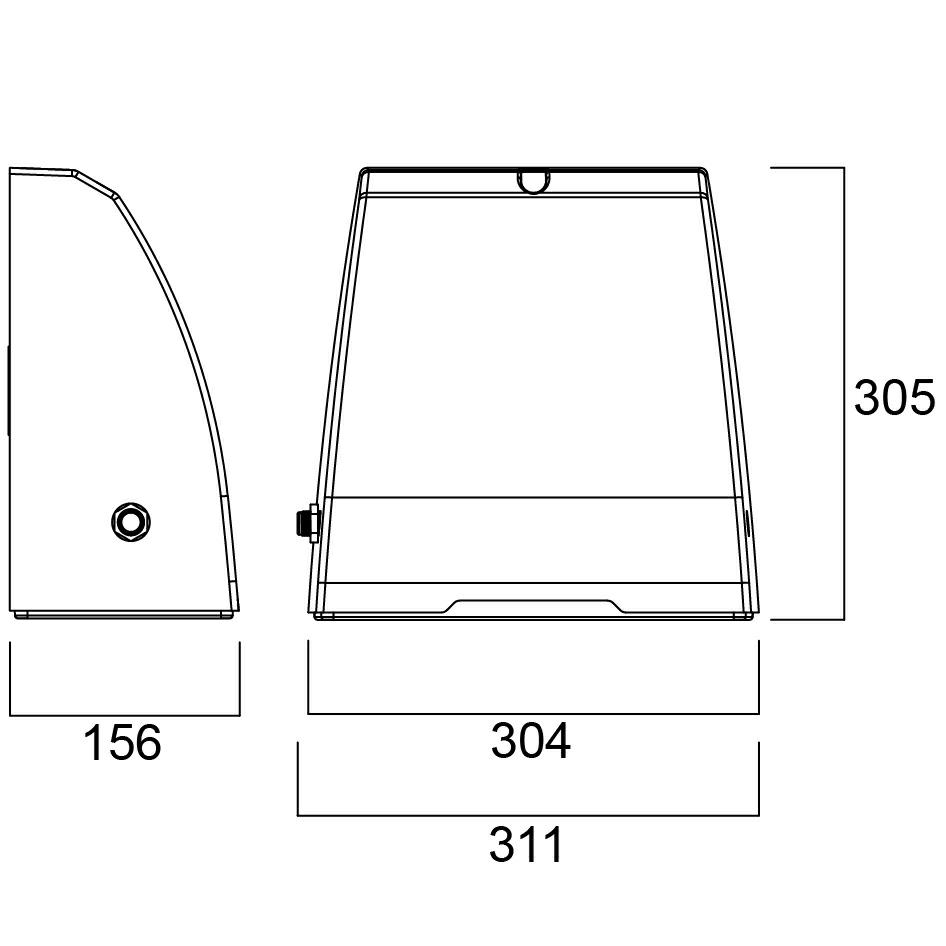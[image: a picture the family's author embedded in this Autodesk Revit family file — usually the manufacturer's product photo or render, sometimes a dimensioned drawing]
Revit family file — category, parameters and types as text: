
# Revit family: 0049945_EM mode
name_source: partatom
category: Lighting Fixtures
revit_build: Autodesk Revit 2018 (Build: 20170223_1515(x64)
units: mm (PartAtom-declared; Revit-internal decimal feet)

## family parameters
Cut with Voids When Loaded = No
Host = Face
Light Source = Yes
OmniClass Number = 23.80.70.00
OmniClass Title = Lighting
Part Type = Normal
Room Calculation Point = No
Round Connector Dimension = Use Diameter
Shared = No

## types (1)
- 0049945 MURO SURF IP65 1700-3250LM 840 PH E3 GR
    Apparent Load = 30 VA
    Assembly Code = D5020200
    AssetType = Fixed
    ClassificationName = Uniclass2015
    ClassificationValue = EF_70_80
    Color Filter = 16777215
    Cost = 0 $
    Default Elevation = 1219 mm
    Description = Muro Surface is a wall mounted fixture for exterior lighting applications with 3 hours combined non-maintained emergency unit. Comes with aluminium housing in RAL7016 anthracite grey colour, frosted PC diffuser, IP65, IK10, Class I, 4000K, non-dimmable multipower driver with 5 settings, 1700 / 1900 / 2750 / 3150 / 3250 lm, 16 / 18 / 26 / 29 / 30 W, up to 109 lm/W total system efficacy, switchable built in Mini photocell, CRI80, Asymmetrical beam, 119.000 hrs L70B50 lifespan, 304 x 305 x 155 mm (L x W x D) dimensions, 4.32 kg weight.
    Dimming Lamp Color Temperature Shift = <None>
    DocumentationLiterature = http://www.sylvania-lighting.com
    ElectricShockClassification = 108
    Emit Shape Visible in Rendering = No
    Emit from Circle Diameter = 610 mm
    IfcExportAs = Class I
    IfcExportType = IfcLightFixtureType
    ImpactProtectionIndex = IfcLightFixtureType
    IngressProtection = IfcLightFixtureType
    InputNominalFrequency = 4000
    InputVoltage = 0
    LampColourRenderingIndex = 16500
    LampColourTemperature = LED
    LampMacAdamStep = 80
    LampNominalLuminous = 4000 K
    LightOutputRatio = LED
    LuminaireType = 0
    ManufacturerName = 108 lm/W
    Material = Feilo Sylvania
    Material_1_SYL = <By Category>
    Material_2_SYL = <By Category>
    Material_3_SYL = <By Category>
    Material_4_SYL = <By Category>
    Model = Muro Surface IP65 1700-3250lm 840 PH E3 Grey
    ModelNumber = 0049945
    ModelReference = Muro Surface IP65 1700-3250lm 840 PH E3 Grey
    Name = Muro Surface IP65 1700-3250lm 840 PH E3 Grey
    NominalDepth = 155 mm  [stored 0.50853 ft]
    NominalHeight = 305 mm  [stored 1.00066 ft]
    NominalLength = 155 mm  [stored 0.50853 ft]
    Photometric Web File = 0049945_EM mode.IES
    PowerConsumption = Lighting
    PowerFactor = 0.95
    Tilt Angle = -90.00°
    Type Image = <None>
    TypeName = Muro Surface IP65 1700-3250lm 840 PH E3 Grey
    URL = 0.9
    Voltage = 0 V
    WarrantyDescription = http://www.sylvania-lighting.com

note: [stored X ft] marks values corroborated as IEEE doubles in the binary element streams (Revit-internal decimal feet)

## geometry (parser evidence)
native form markers: Sweep x2
no freeform markers — native parametric forms only
